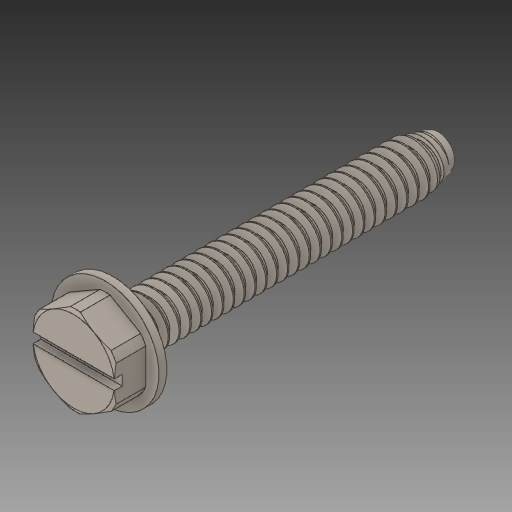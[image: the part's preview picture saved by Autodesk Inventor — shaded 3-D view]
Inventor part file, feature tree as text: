
AUTODESK INVENTOR PART (.ipt)
format: ipt  version: 2017.1 (Build 211199000, 199)  size: 1,202,688 bytes
history: native  units: in
note: dims shown in document units (in); Inventor stores cm internally (conversion verified against a paired STEP export)
features: extrude x1
ambient origin geometry x8: Origin, YZ Plane, XZ Plane, XY Plane, X Axis, Y Axis, Z Axis, Center Point
bodies: Solid1 (feature_tree)
feature tree (1):
  extrude  "Extrude4"  [1 undecoded]
note: 1 required parameter value undecoded (feature->parameter linkage not recoverable at this tier; creation-order binding heuristic only, values carry confidence <= 0.55)
